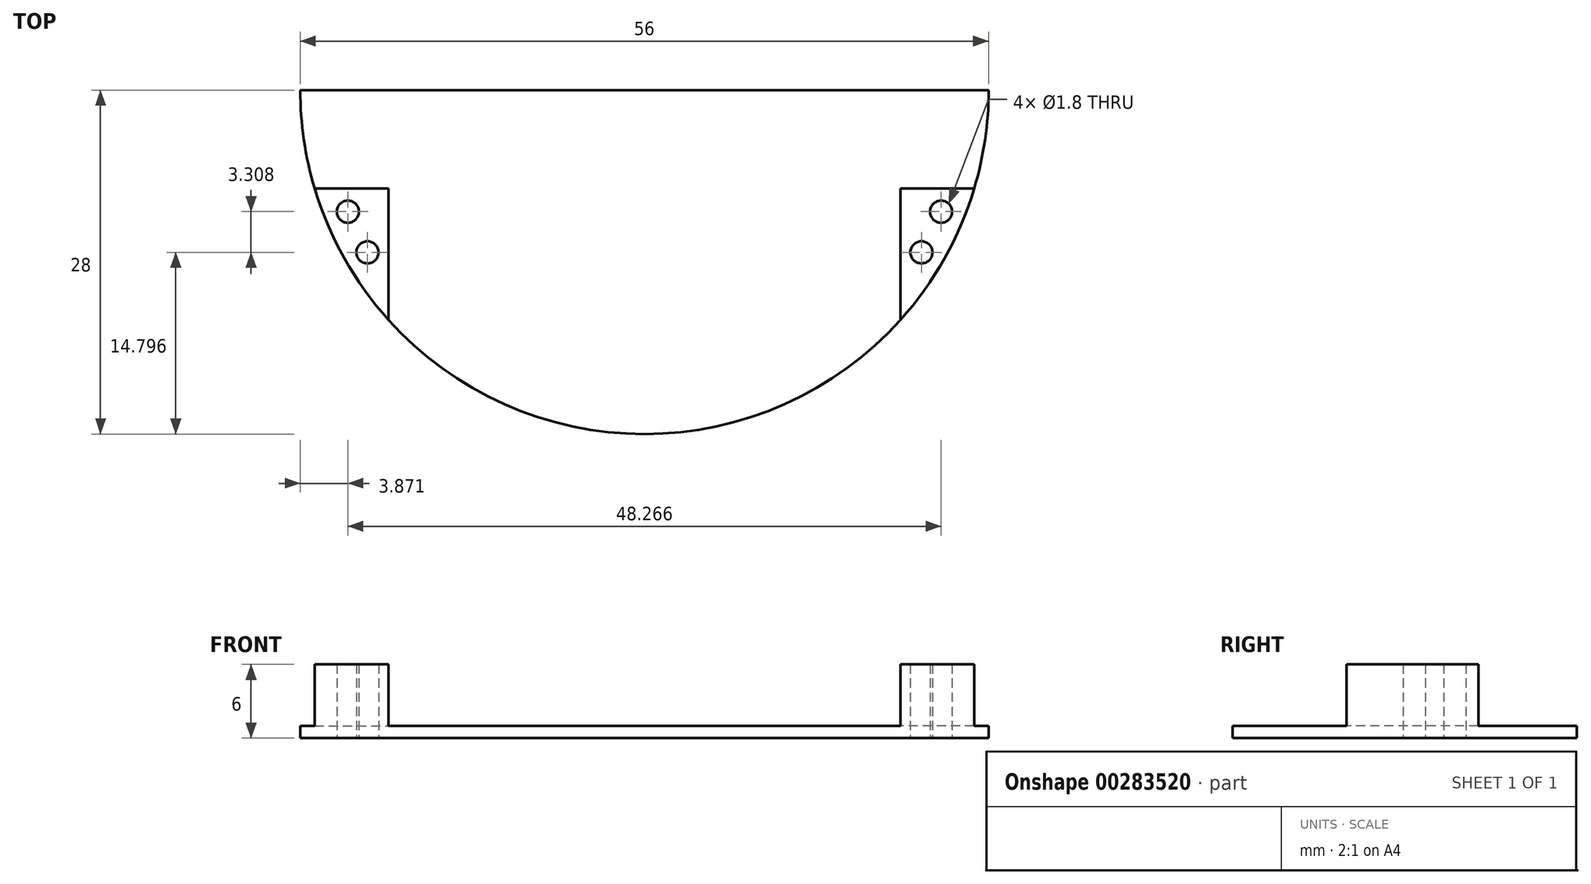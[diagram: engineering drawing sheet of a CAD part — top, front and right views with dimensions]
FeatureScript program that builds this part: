
annotation { "Feature Type Name" : "Feature", "Feature Type Description" : "" }
export const myFeature = defineFeature(function(context is Context, id is Id, definition is map)
    precondition{}
    {
        {
            var Q0;
            Q0=qCreatedBy(makeId("Top.planeOp"),FACE);
            var sketch = newSketch(context, id + "F0", { "sketchPlane" : qUnion([Q0])});
            skCircle(sketch, "E0", {"center": v(-68.19, -113.22) * mm, "radius": 28 * mm});
            skLineSegment(sketch, "E1", {"start": v(-96.19, -113.22) * mm, "end": v(-40.19, -113.22) * mm});
            skSolve(sketch);
        }
        {
            var Q0;
            {var subQ0=sQuery(id+"F0.wireOp",EDGE,"E1");Q0=makeQuery(id+"F0.imprint","IMPRINT",FACE,{"disambiguationData":[TD([[makeQuery(id+"F0.imprint","IMPRINT",EDGE,{"derivedFrom":subQ0}),-1.0]])]});}
            extrude(context, id + "F1", {"entities" : qUnion([Q0]), "depth" : 1 * mm});
        }
        {
            var Q0;
            Q0=makeQuery(id+"F1.opExtrude","CAP_FACE",FACE,{"disambiguationData":[OSD([sQuery(id+"F0.wireOp",EDGE,"E0")])],"isStart":false});
            var sketch = newSketch(context, id + "F2", { "sketchPlane" : qUnion([Q0])});
            skLineSegment(sketch, "E2.bottom", {"start": v(-86.19, -100.91) * mm, "end": v(-50.19, -100.91) * mm, "construction": true});
            skLineSegment(sketch, "E2.top", {"start": v(-86.19, -134.66) * mm, "end": v(-50.19, -134.66) * mm, "construction": true});
            skLineSegment(sketch, "E2.left", {"start": v(-86.19, -100.91) * mm, "end": v(-86.19, -134.66) * mm, "construction": true});
            skLineSegment(sketch, "E2.right", {"start": v(-50.19, -100.91) * mm, "end": v(-50.19, -134.66) * mm, "construction": true});
            skLineSegment(sketch, "E3.top", {"start": v(-86.19, -115.16) * mm, "end": v(-92.69, -115.16) * mm, "construction": true});
            skLineSegment(sketch, "E3.left", {"start": v(-86.19, -112.76) * mm, "end": v(-86.19, -115.16) * mm, "construction": true});
            skLineSegment(sketch, "E3.right", {"start": v(-92.69, -112.76) * mm, "end": v(-92.69, -115.16) * mm, "construction": true});
            skLineSegment(sketch, "E4.top", {"start": v(-50.19, -115.16) * mm, "end": v(-43.69, -115.16) * mm, "construction": true});
            skLineSegment(sketch, "E4.left", {"start": v(-50.19, -112.76) * mm, "end": v(-50.19, -115.16) * mm, "construction": true});
            skLineSegment(sketch, "E4.right", {"start": v(-43.69, -112.76) * mm, "end": v(-43.69, -115.16) * mm, "construction": true});
            skLineSegment(sketch, "E5", {"start": v(-92.69, -112.76) * mm, "end": v(-86.19, -112.76) * mm, "construction": true});
            skLineSegment(sketch, "E6", {"start": v(-50.19, -112.76) * mm, "end": v(-43.69, -112.76) * mm, "construction": true});
            skLineSegment(sketch, "E7", {"start": v(-95.02, -121.22) * mm, "end": v(-89.02, -121.22) * mm});
            skLineSegment(sketch, "E8", {"start": v(-89.02, -121.22) * mm, "end": v(-89.02, -131.92) * mm});
            skLineSegment(sketch, "E9", {"start": v(-41.35, -121.22) * mm, "end": v(-47.35, -121.22) * mm});
            skLineSegment(sketch, "E10", {"start": v(-47.35, -121.22) * mm, "end": v(-47.35, -131.92) * mm});
            skCircle(sketch, "E11", {"center": v(-92.32, -123.12) * mm, "radius": 0.9 * mm});
            skCircle(sketch, "E12", {"center": v(-44.05, -123.12) * mm, "radius": 0.9 * mm});
            skCircle(sketch, "E13", {"center": v(-45.65, -126.42) * mm, "radius": 0.9 * mm});
            skCircle(sketch, "E14", {"center": v(-90.72, -126.42) * mm, "radius": 0.9 * mm});
            skSolve(sketch);
        }
        {
            var Q0;
            {var subQ1=sQuery(id+"F2.wireOp",EDGE,"E7");Q0=makeQuery(id+"F2.imprint","IMPRINT",FACE,{"disambiguationData":[TD([[makeQuery(id+"F2.imprint","IMPRINT",EDGE,{"derivedFrom":subQ1}),-1.0]])]});}
            var Q1;
            {var subQ1=sQuery(id+"F2.wireOp",EDGE,"E9");Q1=makeQuery(id+"F2.imprint","IMPRINT",FACE,{"disambiguationData":[TD([[makeQuery(id+"F2.imprint","IMPRINT",EDGE,{"derivedFrom":subQ1}),1.0]])]});}
            extrude(context, id + "F3", {"entities" : qUnion([Q0, Q1]), "operationType" : NewBodyOperationType.ADD, "depth" : 5 * mm});
        }
        {
            var Q0;
            Q0=makeQuery(id+"F2.imprint","IMPRINT",FACE,{"disambiguationData":[TD([[makeQuery(id+"F2.imprint","IMPRINT",EDGE,{"derivedFrom":sQuery(id+"F2.wireOp",EDGE,"E11")}),1.0]])]});
            var Q1;
            Q1=makeQuery(id+"F2.imprint","IMPRINT",FACE,{"disambiguationData":[TD([[makeQuery(id+"F2.imprint","IMPRINT",EDGE,{"derivedFrom":sQuery(id+"F2.wireOp",EDGE,"E14")}),1.0]])]});
            var Q2;
            Q2=makeQuery(id+"F2.imprint","IMPRINT",FACE,{"disambiguationData":[TD([[makeQuery(id+"F2.imprint","IMPRINT",EDGE,{"derivedFrom":sQuery(id+"F2.wireOp",EDGE,"E12")}),1.0]])]});
            var Q3;
            Q3=makeQuery(id+"F2.imprint","IMPRINT",FACE,{"disambiguationData":[TD([[makeQuery(id+"F2.imprint","IMPRINT",EDGE,{"derivedFrom":sQuery(id+"F2.wireOp",EDGE,"E13")}),1.0]])]});
            extrude(context, id + "F4", {"entities" : qUnion([Q0, Q1, Q2, Q3]), "operationType" : NewBodyOperationType.REMOVE, "endBound" : BoundingType.THROUGH_ALL, "oppositeDirection" : true, "depth" : 25 * mm});
        }
    });
